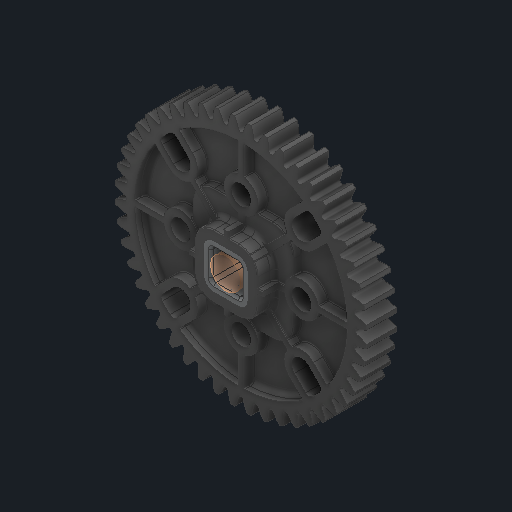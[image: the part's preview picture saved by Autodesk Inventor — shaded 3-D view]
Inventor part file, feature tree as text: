
AUTODESK INVENTOR PART (.ipt)
format: ipt  version: 2025 (Build 290162000, 162)  size: 3,641,344 bytes
history: native  units: in
note: dims shown in document units (in); Inventor stores cm internally (conversion verified against a paired STEP export)
features: other x6, sketch x3
ambient origin geometry x8: Origin, YZ Plane, XZ Plane, XY Plane, X Axis, Y Axis, Z Axis, Center Point
bodies: Solid1 (feature_tree), Solid2 (feature_tree)
feature tree (9):
  other  "Half Cut HS 48T Gear, No Insert.ipt"
  other  "Solid1::Half Cut HS 48T Gear, No Insert.ipt"
  other  "Solid2::Half Cut HS 48T Gear, No Insert.ipt"
  other  "TaggingFeature1"
  sketch  "Sketch1"  dims[d0=0.3937in]
  sketch  "Sketch2"
  sketch  "Sketch3"
  other  "Srf1"
  other  "Srf1::Derived"
